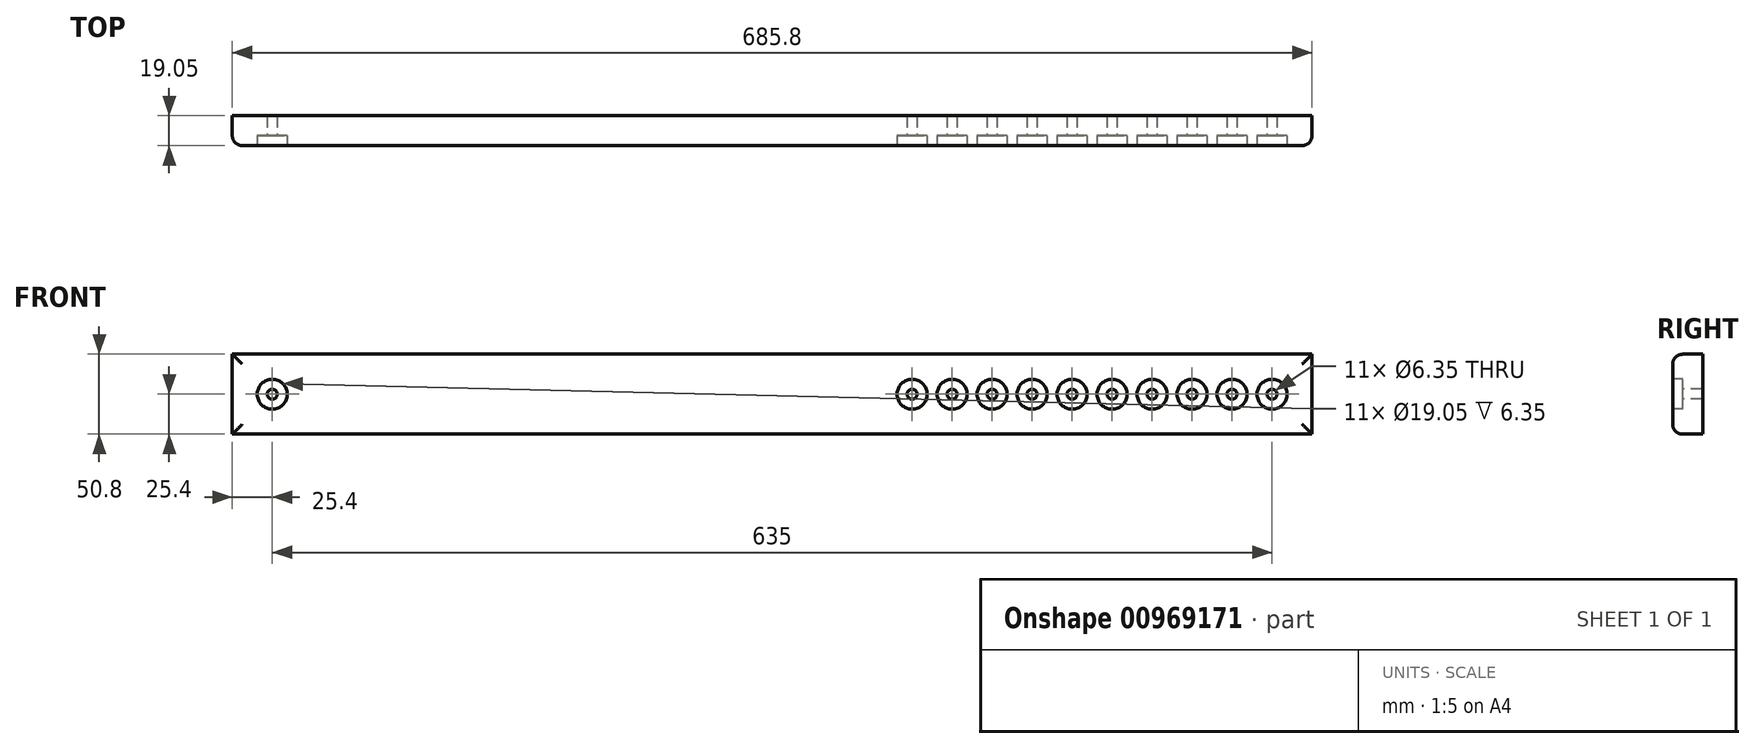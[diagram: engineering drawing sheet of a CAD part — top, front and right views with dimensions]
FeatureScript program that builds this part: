
annotation { "Feature Type Name" : "Feature", "Feature Type Description" : "" }
export const myFeature = defineFeature(function(context is Context, id is Id, definition is map)
    precondition{}
    {
        {
            var Q0;
            Q0=qCreatedBy(makeId("Front.planeOp"),FACE);
            var sketch = newSketch(context, id + "F0", { "sketchPlane" : qUnion([Q0])});
            skLineSegment(sketch, "E0.bottom", {"start": v(342.9, -25.4) * mm, "end": v(-342.9, -25.4) * mm});
            skLineSegment(sketch, "E0.top", {"start": v(342.9, 25.4) * mm, "end": v(-342.9, 25.4) * mm});
            skLineSegment(sketch, "E0.left", {"start": v(342.9, -25.4) * mm, "end": v(342.9, 25.4) * mm});
            skLineSegment(sketch, "E0.right", {"start": v(-342.9, -25.4) * mm, "end": v(-342.9, 25.4) * mm});
            skPoint(sketch, "E0.middle", {"position": v(0, 0) * mm});
            skSolve(sketch);
        }
        {
            var Q0;
            Q0=makeQuery(id+"F0.imprint","IMPRINT",FACE,{"disambiguationData":[TD([[makeQuery(id+"F0.imprint","IMPRINT",EDGE,{"derivedFrom":sQuery(id+"F0.wireOp",EDGE,"E0.bottom")}),-1.0]])]});
            extrude(context, id + "F1", {"entities" : qUnion([Q0]), "depth" : 19.05 * mm, "offsetDistance" : 25.4 * mm});
        }
        {
            var Q0;
            Q0=makeQuery(id+"F1.opExtrude","CAP_FACE",FACE,{"disambiguationData":[OSD([sQuery(id+"F0.wireOp",EDGE,"E0.bottom"),sQuery(id+"F0.wireOp",EDGE,"E0.top"),sQuery(id+"F0.wireOp",EDGE,"E0.left"),sQuery(id+"F0.wireOp",EDGE,"E0.right")])],"isStart":false});
            var sketch = newSketch(context, id + "F2", { "sketchPlane" : qUnion([Q0])});
            skPoint(sketch, "E1", {"position": v(-317.5, 0) * mm});
            skSolve(sketch);
        }
        {
            var Q0;
            Q0=sQuery(id+"F2.wireOp",VERTEX,"E1");
            var Q1;
            Q1=makeQuery(id+"F1.opExtrude","SWEPT_BODY",BODY,{"disambiguationData":[OSD([sQuery(id+"F0.wireOp",EDGE,"E0.bottom"),sQuery(id+"F0.wireOp",EDGE,"E0.top"),sQuery(id+"F0.wireOp",EDGE,"E0.left"),sQuery(id+"F0.wireOp",EDGE,"E0.right")])]});
            hole(context, id + "F3", {"style" : HoleStyle.C_BORE, "endStyle" : HoleEndStyle.THROUGH, "holeDiameter" : 6.35 * mm, "cBoreDiameter" : 19.05 * mm, "cBoreDepth" : 6.35 * mm, "majorDiameter" : 6.35 * mm, "isTappedThrough" : true, "tappedDepth" : 12.7 * mm, "tapClearance" : 3, "locations" : qUnion([Q0]), "scope" : qUnion([Q1])});
        }
        {
            var Q0;
            Q0=makeQuery(id+"F1.opExtrude","CAP_FACE",FACE,{"disambiguationData":[OSD([sQuery(id+"F0.wireOp",EDGE,"E0.bottom"),sQuery(id+"F0.wireOp",EDGE,"E0.top"),sQuery(id+"F0.wireOp",EDGE,"E0.left"),sQuery(id+"F0.wireOp",EDGE,"E0.right")])],"isStart":false});
            var sketch = newSketch(context, id + "F4", { "sketchPlane" : qUnion([Q0])});
            skPoint(sketch, "E2", {"position": v(317.5, 0) * mm});
            skPoint(sketch, "E3.1.0.0", {"position": v(292.1, 0) * mm});
            skPoint(sketch, "E3.2.0.0", {"position": v(266.7, 0) * mm});
            skPoint(sketch, "E3.3.0.0", {"position": v(241.3, 0) * mm});
            skPoint(sketch, "E3.4.0.0", {"position": v(215.9, 0) * mm});
            skPoint(sketch, "E3.5.0.0", {"position": v(190.5, 0) * mm});
            skPoint(sketch, "E3.6.0.0", {"position": v(165.1, 0) * mm});
            skPoint(sketch, "E3.7.0.0", {"position": v(139.7, 0) * mm});
            skPoint(sketch, "E3.8.0.0", {"position": v(114.3, 0) * mm});
            skPoint(sketch, "E3.9.0.0", {"position": v(88.9, 0) * mm});
            skLineSegment(sketch, "E3.direction1", {"start": v(317.5, 0) * mm, "end": v(292.1, 0) * mm, "construction": true});
            skSolve(sketch);
        }
        {
            var Q0;
            Q0=sQuery(id+"F4.wireOp",VERTEX,"E2");
            var Q1;
            Q1=sQuery(id+"F4.wireOp",VERTEX,"E3.1.0.0");
            var Q2;
            Q2=sQuery(id+"F4.wireOp",VERTEX,"E3.2.0.0");
            var Q3;
            Q3=sQuery(id+"F4.wireOp",VERTEX,"E3.3.0.0");
            var Q4;
            Q4=sQuery(id+"F4.wireOp",VERTEX,"E3.4.0.0");
            var Q5;
            Q5=sQuery(id+"F4.wireOp",VERTEX,"E3.5.0.0");
            var Q6;
            Q6=sQuery(id+"F4.wireOp",VERTEX,"E3.6.0.0");
            var Q7;
            Q7=sQuery(id+"F4.wireOp",VERTEX,"E3.7.0.0");
            var Q8;
            Q8=sQuery(id+"F4.wireOp",VERTEX,"E3.8.0.0");
            var Q9;
            Q9=sQuery(id+"F4.wireOp",VERTEX,"E3.9.0.0");
            var Q10;
            Q10=makeQuery(id+"F1.opExtrude","SWEPT_BODY",BODY,{"disambiguationData":[OSD([sQuery(id+"F0.wireOp",EDGE,"E0.bottom"),sQuery(id+"F0.wireOp",EDGE,"E0.top"),sQuery(id+"F0.wireOp",EDGE,"E0.left"),sQuery(id+"F0.wireOp",EDGE,"E0.right")])]});
            hole(context, id + "F5", {"style" : HoleStyle.C_BORE, "endStyle" : HoleEndStyle.THROUGH, "holeDiameter" : 6.35 * mm, "cBoreDiameter" : 19.05 * mm, "cBoreDepth" : 6.35 * mm, "majorDiameter" : 6.35 * mm, "isTappedThrough" : true, "tappedDepth" : 12.7 * mm, "tapClearance" : 3, "locations" : qUnion([Q0, Q1, Q2, Q3, Q4, Q5, Q6, Q7, Q8, Q9]), "scope" : qUnion([Q10])});
        }
        {
            var Q0;
            Q0=makeQuery(id+"F1.opExtrude","CAP_EDGE",EDGE,{"disambiguationData":[OSD([sQuery(id+"F0.wireOp",EDGE,"E0.top")])],"isStart":false});
            var Q1;
            Q1=makeQuery(id+"F1.opExtrude","CAP_EDGE",EDGE,{"disambiguationData":[OSD([sQuery(id+"F0.wireOp",EDGE,"E0.right")])],"isStart":false});
            var Q2;
            Q2=makeQuery(id+"F1.opExtrude","CAP_EDGE",EDGE,{"disambiguationData":[OSD([sQuery(id+"F0.wireOp",EDGE,"E0.bottom")])],"isStart":false});
            var Q3;
            Q3=makeQuery(id+"F1.opExtrude","CAP_EDGE",EDGE,{"disambiguationData":[OSD([sQuery(id+"F0.wireOp",EDGE,"E0.left")])],"isStart":false});
            fillet(context, id + "F6", {"entities" : qUnion([Q0, Q1, Q2, Q3]), "radius" : 6.35 * mm, "tangentPropagation" : true, "allowEdgeOverflow" : false});
        }
    });
